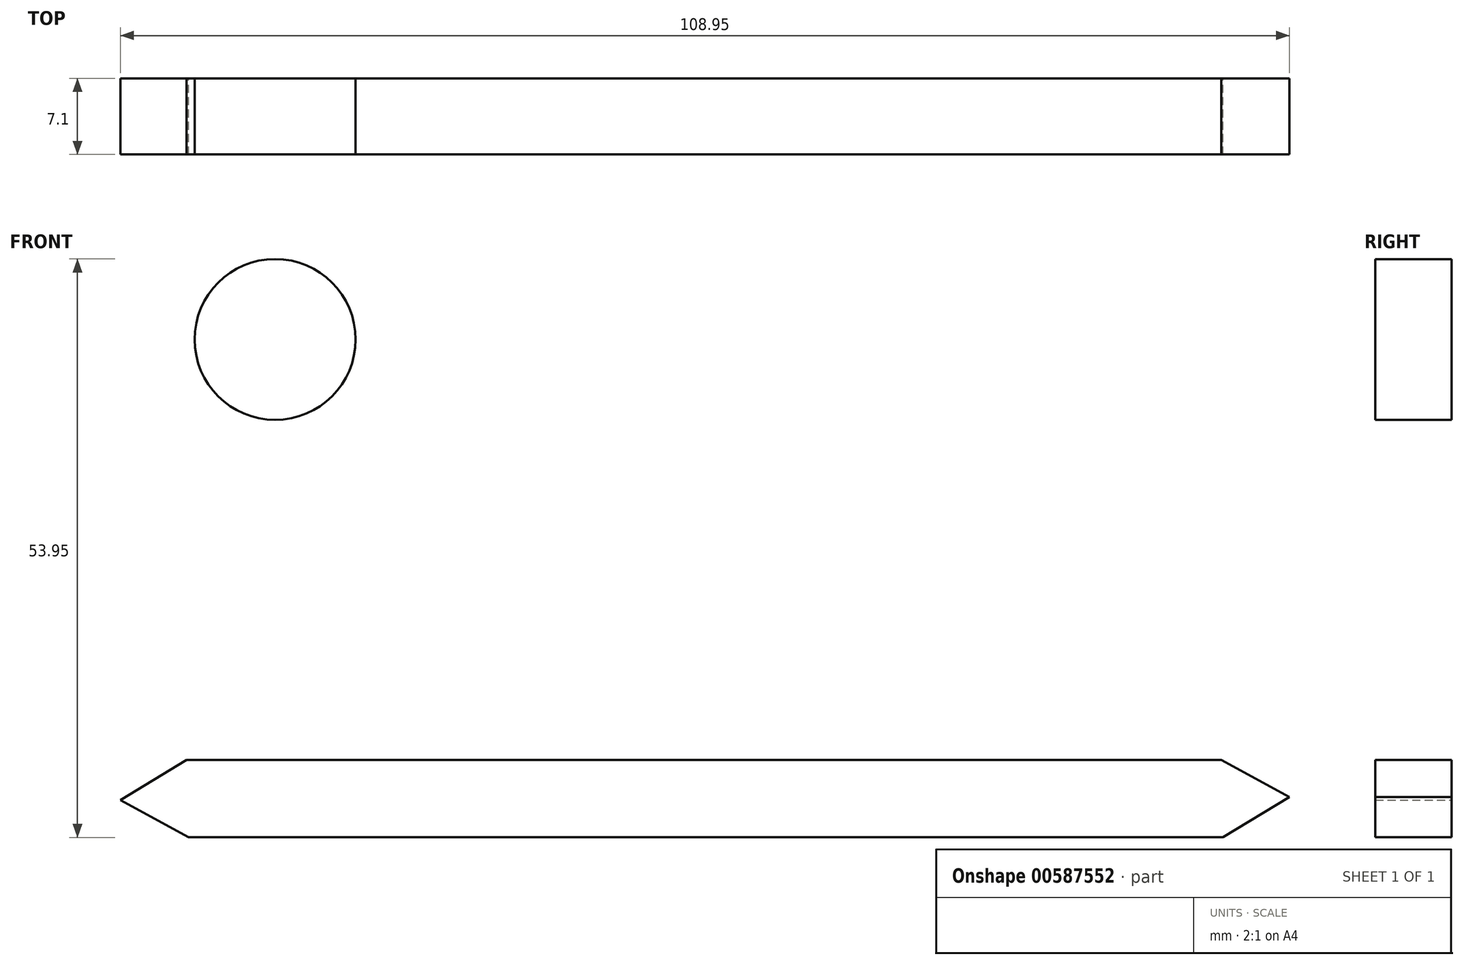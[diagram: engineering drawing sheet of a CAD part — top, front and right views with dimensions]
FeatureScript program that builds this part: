
annotation { "Feature Type Name" : "Feature", "Feature Type Description" : "" }
export const myFeature = defineFeature(function(context is Context, id is Id, definition is map)
    precondition{}
    {
        {
            var Q0;
            Q0=qCreatedBy(makeId("Front.planeOp"),FACE);
            var sketch = newSketch(context, id + "F0", { "sketchPlane" : qUnion([Q0])});
            skCircle(sketch, "E0", {"center": v(-22.46, 15.4) * mm, "radius": 7.5 * mm});
            skLineSegment(sketch, "E1", {"start": v(-30.54, -31.05) * mm, "end": v(65.88, -31.05) * mm});
            skLineSegment(sketch, "E2", {"start": v(65.88, -31.05) * mm, "end": v(72.06, -27.28) * mm});
            skLineSegment(sketch, "E3", {"start": v(72.06, -27.28) * mm, "end": v(65.7, -23.81) * mm});
            skLineSegment(sketch, "E4", {"start": v(65.7, -23.81) * mm, "end": v(65.88, -31.05) * mm});
            skLineSegment(sketch, "E5", {"start": v(65.7, -23.81) * mm, "end": v(-30.7, -23.81) * mm});
            skLineSegment(sketch, "E6", {"start": v(-30.7, -23.81) * mm, "end": v(-36.9, -27.57) * mm});
            skLineSegment(sketch, "E7", {"start": v(-36.9, -27.57) * mm, "end": v(-30.54, -31.05) * mm});
            skLineSegment(sketch, "E8", {"start": v(-30.54, -31.05) * mm, "end": v(-30.7, -23.81) * mm});
            skSolve(sketch);
        }
        {
            var Q0;
            Q0 = qSketchRegion(id + "F0", true);
            extrude(context, id + "F1", {"entities" : qUnion([Q0]), "depth" : 7.1 * mm, "offsetDistance" : 25 * mm});
        }
    });
